# Revit family: Faucet-Sidespray-Kitchen-KOHLER-Accent-K-10101_1
name_source: partatom
category: Plumbing Fixtures
revit_build: Autodesk Revit 2017 (Build: 20160225_1515(x64)
units: mm (PartAtom-declared; Revit-internal decimal feet)

## family parameters
Cut with Voids When Loaded = No
Host = Face
OmniClass Number = 23.31.11.00
OmniClass Title = Faucets
Part Type = Normal
Room Calculation Point = No
Round Connector Dimension = Use Diameter
Shared = No

## types (6) — shared parameters
ADA Compliant = No
Assembly Code = D2010
CW Connection = Yes
Cold Water Inlet = Cold Water Inlet
Date Modified = 01/29/2021
Default Elevation = 36"
Description = Kitchen Sidespray
Drain Included = No
Faucet Hole Spacing = 0"
Flow Rate = 0 GPM
HW Connection = No
Handle Clearance = 0"
Height = 5 3/4"
Hot Water Inlet = Hot Water Inlet
Length = 1 3/4"
Manufacturer = KOHLER Co.
Master Format 2014 = 22 41 39
Master Format 2014 Name = Residential Faucets, Supplies, and Trim
Material = Premium Metal Constriction
Pressure = 0.00 psi
Product Documentation Link = https://www.us.kohler.com
Product Name = Accent
Product Page URL = http://www.us.kohler.com
Spout Reach = 0"
URL = https://www.us.kohler.com
Vent Connection = No
Waste Connection = No
Waste Water Outlet = Waste Water Outlet
WaterSense Certified = No
Width = 1 3/4"

## per-type parameters (varying)
| type | Finish | Model | Type |
| CP - Polished Chrome | Kohler-Metal-CP-Polished_Chrome | K-10101-CP | 1 |
| AF - Vibrant French Gold | Kohler-Metal-AF-Vibrant_French_Gold | K-10101-AF | 2 |
| PB - Vibrant Polished Brass | Kohler-Metal-PB-Vibrant_Polished_Brass | K-10101-PB | 3 |
| BN - Vibrant Brushed Nickel | Kohler-Metal-BN-Vibrant_Brushed_Nickel | K-10101-BN | 4 |
| BV - Vibrant Brushed Bronze | Kohler-Metal-BV-Brushed_Bronze | K-10101-BV | 5 |
| 2BZ - Oil-Rubbed Bronze | Kohler-Metal-2BZ-Oil_Rubbed_Bronze | K-10101-2BZ | 6 |

## geometry (parser evidence)
native form markers: Sweep x5
no freeform markers — native parametric forms only
